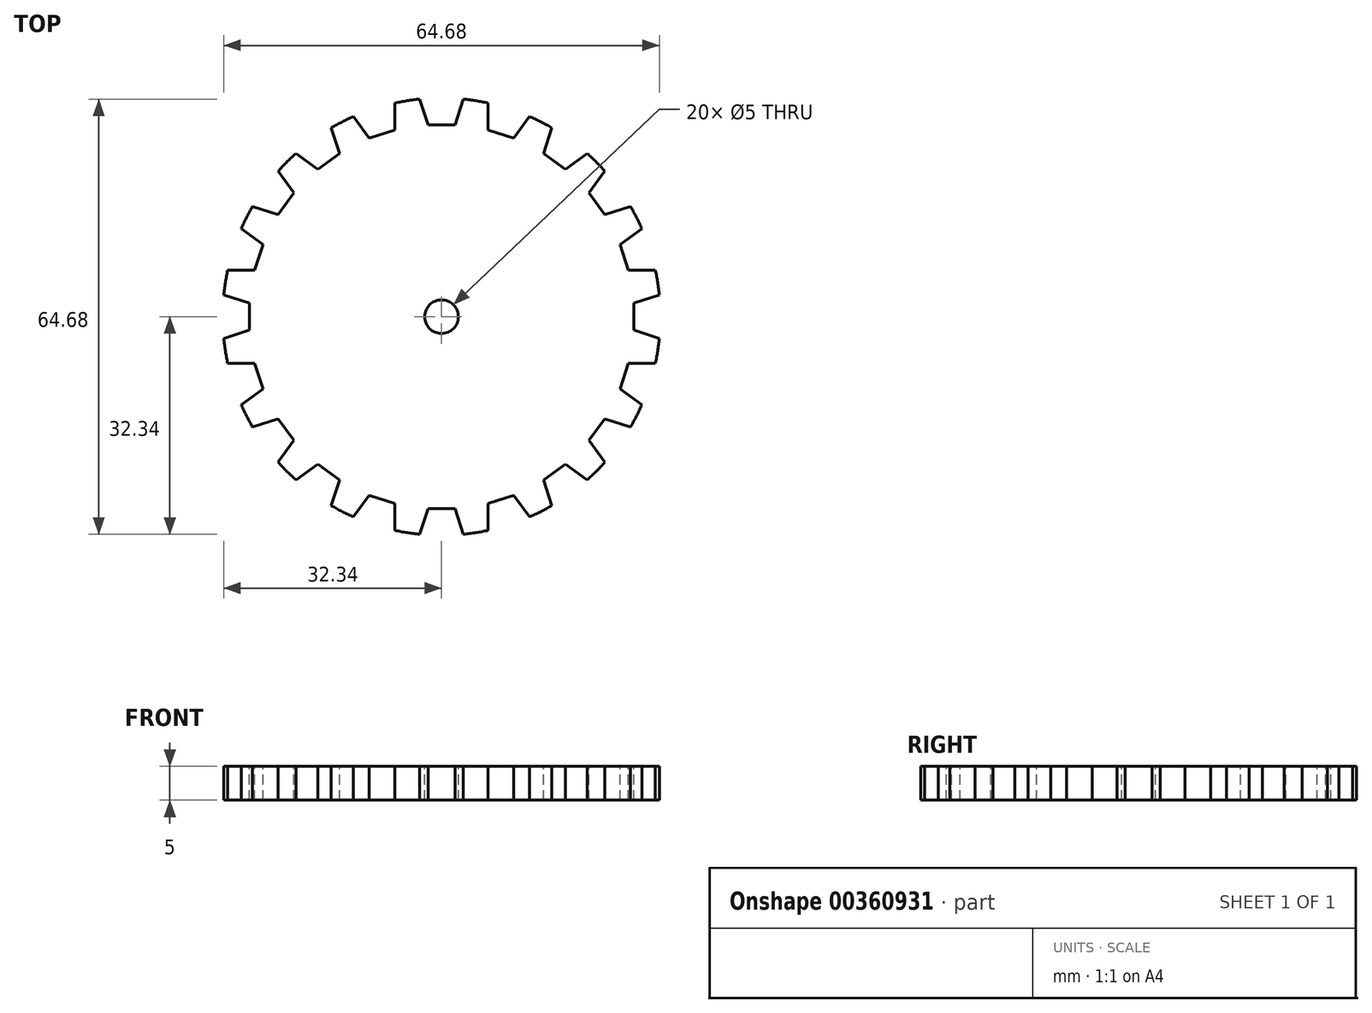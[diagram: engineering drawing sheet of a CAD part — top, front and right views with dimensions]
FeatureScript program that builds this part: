
annotation { "Feature Type Name" : "Feature", "Feature Type Description" : "" }
export const myFeature = defineFeature(function(context is Context, id is Id, definition is map)
    precondition{}
    {
        {
            var Q0;
            Q0=qCreatedBy(makeId("Top.planeOp"),FACE);
            var sketch = newSketch(context, id + "F0", { "sketchPlane" : qUnion([Q0])});
            skCircle(sketch, "E0", {"center": v(0, 0) * mm, "radius": 32.5 * mm});
            skSolve(sketch);
        }
        {
            var Q0;
            Q0=makeQuery(id+"F0.imprint","IMPRINT",FACE,{"disambiguationData":[TD([[makeQuery(id+"F0.imprint","IMPRINT",EDGE,{"derivedFrom":sQuery(id+"F0.wireOp",EDGE,"E0")}),1.0]])]});
            extrude(context, id + "F1", {"entities" : qUnion([Q0]), "depth" : 5 * mm});
        }
        {
            var Q0;
            Q0=makeQuery(id+"F1.opExtrude","CAP_FACE",FACE,{"disambiguationData":[OSD([sQuery(id+"F0.wireOp",EDGE,"E0")])],"isStart":false});
            var sketch = newSketch(context, id + "F2", { "sketchPlane" : qUnion([Q0])});
            skLineSegment(sketch, "E1", {"start": v(3.24, 32.34) * mm, "end": v(2, 28.53) * mm});
            skLineSegment(sketch, "E2", {"start": v(2, 28.53) * mm, "end": v(0, 28.53) * mm});
            skLineSegment(sketch, "E3.MirrorCS", {"start": v(-3.24, 32.34) * mm, "end": v(-2, 28.53) * mm});
            skLineSegment(sketch, "E4.MirrorCS", {"start": v(-2, 28.53) * mm, "end": v(0, 28.53) * mm});
            skArc(sketch, "E5", {"start": v(3.24, 32.34) * mm, "mid": v(0, 34.14) * mm, "end": v(-3.24, 32.34) * mm});
            skSolve(sketch);
        }
        {
            var Q0;
            {var subQ0=sQuery(id+"F2.wireOp",EDGE,"E5");Q0=makeQuery(id+"F2.imprint","IMPRINT",FACE,{"disambiguationData":[TD([[makeQuery(id+"F2.imprint","IMPRINT",EDGE,{"derivedFrom":subQ0}),1.0]])]});}
            var Q1;
            {var subQ1=sQuery(id+"F2.wireOp",EDGE,"E1");Q1=makeQuery(id+"F2.imprint","IMPRINT",FACE,{"disambiguationData":[TD([[makeQuery(id+"F2.imprint","IMPRINT",EDGE,{"derivedFrom":subQ1}),-1.0]])]});}
            extrude(context, id + "F3", {"entities" : qUnion([Q0, Q1]), "operationType" : NewBodyOperationType.ADD, "depth" : 10 * mm});
        }
        {
            var Q0;
            Q0=makeQuery(id+"F1.opExtrude","CAP_FACE",FACE,{"disambiguationData":[OSD([sQuery(id+"F0.wireOp",EDGE,"E0")])],"isStart":false});
            var sketch = newSketch(context, id + "F4", { "sketchPlane" : qUnion([Q0])});
            skCircle(sketch, "E6", {"center": v(0, 0) * mm, "radius": 2.5 * mm});
            skSolve(sketch);
        }
        {
            var Q0;
            Q0=makeQuery(id+"F4.imprint","IMPRINT",FACE,{"disambiguationData":[TD([[makeQuery(id+"F4.imprint","IMPRINT",EDGE,{"derivedFrom":sQuery(id+"F4.wireOp",EDGE,"E6")}),1.0]])]});
            extrude(context, id + "F5", {"entities" : qUnion([Q0]), "operationType" : NewBodyOperationType.REMOVE, "oppositeDirection" : true, "depth" : 25 * mm});
        }
        {
            var Q0;
            Q0=makeQuery(id+"F1.opExtrude","SWEPT_BODY",BODY,{"disambiguationData":[OSD([sQuery(id+"F0.wireOp",EDGE,"E0")])]});
            var Q1;
            Q1=makeQuery(id+"F5.boolean.opBoolean","COPY",FACE,{"derivedFrom":makeQuery(id+"F5.opExtrude","SWEPT_FACE",FACE,{"disambiguationData":[OSD([sQuery(id+"F4.wireOp",EDGE,"E6")])]})});
            circularPattern(context, id + "F6", {"entities" : qUnion([Q0]), "axis" : qUnion([Q1]), "angle" : 360 * degree, "instanceCount" : 20, "equalSpace" : true});
        }
        {
            var Q0;
            Q0=makeQuery(id+"F6.opPattern","COPY",FACE,{"derivedFrom":makeQuery(id+"F3.opExtrude","CAP_FACE",FACE,{"disambiguationData":[OSD([sQuery(id+"F2.wireOp",EDGE,"E1"),sQuery(id+"F2.wireOp",EDGE,"E2"),sQuery(id+"F2.wireOp",EDGE,"E3.MirrorCS"),sQuery(id+"F2.wireOp",EDGE,"E4.MirrorCS"),sQuery(id+"F2.wireOp",EDGE,"E5")])],"isStart":false}),"instanceName":"16"});
            var Q1;
            Q1=makeQuery(id+"F6.opPattern","COPY",FACE,{"derivedFrom":makeQuery(id+"F3.opExtrude","CAP_FACE",FACE,{"disambiguationData":[OSD([sQuery(id+"F2.wireOp",EDGE,"E1"),sQuery(id+"F2.wireOp",EDGE,"E2"),sQuery(id+"F2.wireOp",EDGE,"E3.MirrorCS"),sQuery(id+"F2.wireOp",EDGE,"E4.MirrorCS"),sQuery(id+"F2.wireOp",EDGE,"E5")])],"isStart":false}),"instanceName":"17"});
            var Q2;
            Q2=makeQuery(id+"F6.opPattern","COPY",FACE,{"derivedFrom":makeQuery(id+"F3.opExtrude","CAP_FACE",FACE,{"disambiguationData":[OSD([sQuery(id+"F2.wireOp",EDGE,"E1"),sQuery(id+"F2.wireOp",EDGE,"E2"),sQuery(id+"F2.wireOp",EDGE,"E3.MirrorCS"),sQuery(id+"F2.wireOp",EDGE,"E4.MirrorCS"),sQuery(id+"F2.wireOp",EDGE,"E5")])],"isStart":false}),"instanceName":"18"});
            var Q3;
            Q3=makeQuery(id+"F6.opPattern","COPY",FACE,{"derivedFrom":makeQuery(id+"F3.opExtrude","CAP_FACE",FACE,{"disambiguationData":[OSD([sQuery(id+"F2.wireOp",EDGE,"E1"),sQuery(id+"F2.wireOp",EDGE,"E2"),sQuery(id+"F2.wireOp",EDGE,"E3.MirrorCS"),sQuery(id+"F2.wireOp",EDGE,"E4.MirrorCS"),sQuery(id+"F2.wireOp",EDGE,"E5")])],"isStart":false}),"instanceName":"19"});
            var Q4;
            Q4=makeQuery(id+"F3.opExtrude","CAP_FACE",FACE,{"disambiguationData":[OSD([sQuery(id+"F2.wireOp",EDGE,"E1"),sQuery(id+"F2.wireOp",EDGE,"E2"),sQuery(id+"F2.wireOp",EDGE,"E3.MirrorCS"),sQuery(id+"F2.wireOp",EDGE,"E4.MirrorCS"),sQuery(id+"F2.wireOp",EDGE,"E5")])],"isStart":false});
            var Q5;
            Q5=makeQuery(id+"F6.opPattern","COPY",FACE,{"derivedFrom":makeQuery(id+"F3.opExtrude","CAP_FACE",FACE,{"disambiguationData":[OSD([sQuery(id+"F2.wireOp",EDGE,"E1"),sQuery(id+"F2.wireOp",EDGE,"E2"),sQuery(id+"F2.wireOp",EDGE,"E3.MirrorCS"),sQuery(id+"F2.wireOp",EDGE,"E4.MirrorCS"),sQuery(id+"F2.wireOp",EDGE,"E5")])],"isStart":false}),"instanceName":"1"});
            var Q6;
            Q6=makeQuery(id+"F6.opPattern","COPY",FACE,{"derivedFrom":makeQuery(id+"F3.opExtrude","CAP_FACE",FACE,{"disambiguationData":[OSD([sQuery(id+"F2.wireOp",EDGE,"E1"),sQuery(id+"F2.wireOp",EDGE,"E2"),sQuery(id+"F2.wireOp",EDGE,"E3.MirrorCS"),sQuery(id+"F2.wireOp",EDGE,"E4.MirrorCS"),sQuery(id+"F2.wireOp",EDGE,"E5")])],"isStart":false}),"instanceName":"2"});
            var Q7;
            Q7=makeQuery(id+"F6.opPattern","COPY",FACE,{"derivedFrom":makeQuery(id+"F3.opExtrude","CAP_FACE",FACE,{"disambiguationData":[OSD([sQuery(id+"F2.wireOp",EDGE,"E1"),sQuery(id+"F2.wireOp",EDGE,"E2"),sQuery(id+"F2.wireOp",EDGE,"E3.MirrorCS"),sQuery(id+"F2.wireOp",EDGE,"E4.MirrorCS"),sQuery(id+"F2.wireOp",EDGE,"E5")])],"isStart":false}),"instanceName":"3"});
            var Q8;
            Q8=makeQuery(id+"F6.opPattern","COPY",FACE,{"derivedFrom":makeQuery(id+"F3.opExtrude","CAP_FACE",FACE,{"disambiguationData":[OSD([sQuery(id+"F2.wireOp",EDGE,"E1"),sQuery(id+"F2.wireOp",EDGE,"E2"),sQuery(id+"F2.wireOp",EDGE,"E3.MirrorCS"),sQuery(id+"F2.wireOp",EDGE,"E4.MirrorCS"),sQuery(id+"F2.wireOp",EDGE,"E5")])],"isStart":false}),"instanceName":"4"});
            var Q9;
            Q9=makeQuery(id+"F6.opPattern","COPY",FACE,{"derivedFrom":makeQuery(id+"F3.opExtrude","CAP_FACE",FACE,{"disambiguationData":[OSD([sQuery(id+"F2.wireOp",EDGE,"E1"),sQuery(id+"F2.wireOp",EDGE,"E2"),sQuery(id+"F2.wireOp",EDGE,"E3.MirrorCS"),sQuery(id+"F2.wireOp",EDGE,"E4.MirrorCS"),sQuery(id+"F2.wireOp",EDGE,"E5")])],"isStart":false}),"instanceName":"5"});
            var Q10;
            Q10=makeQuery(id+"F6.opPattern","COPY",FACE,{"derivedFrom":makeQuery(id+"F3.opExtrude","CAP_FACE",FACE,{"disambiguationData":[OSD([sQuery(id+"F2.wireOp",EDGE,"E1"),sQuery(id+"F2.wireOp",EDGE,"E2"),sQuery(id+"F2.wireOp",EDGE,"E3.MirrorCS"),sQuery(id+"F2.wireOp",EDGE,"E4.MirrorCS"),sQuery(id+"F2.wireOp",EDGE,"E5")])],"isStart":false}),"instanceName":"6"});
            var Q11;
            Q11=makeQuery(id+"F6.opPattern","COPY",FACE,{"derivedFrom":makeQuery(id+"F3.opExtrude","CAP_FACE",FACE,{"disambiguationData":[OSD([sQuery(id+"F2.wireOp",EDGE,"E1"),sQuery(id+"F2.wireOp",EDGE,"E2"),sQuery(id+"F2.wireOp",EDGE,"E3.MirrorCS"),sQuery(id+"F2.wireOp",EDGE,"E4.MirrorCS"),sQuery(id+"F2.wireOp",EDGE,"E5")])],"isStart":false}),"instanceName":"7"});
            var Q12;
            Q12=makeQuery(id+"F6.opPattern","COPY",FACE,{"derivedFrom":makeQuery(id+"F3.opExtrude","CAP_FACE",FACE,{"disambiguationData":[OSD([sQuery(id+"F2.wireOp",EDGE,"E1"),sQuery(id+"F2.wireOp",EDGE,"E2"),sQuery(id+"F2.wireOp",EDGE,"E3.MirrorCS"),sQuery(id+"F2.wireOp",EDGE,"E4.MirrorCS"),sQuery(id+"F2.wireOp",EDGE,"E5")])],"isStart":false}),"instanceName":"8"});
            var Q13;
            Q13=makeQuery(id+"F6.opPattern","COPY",FACE,{"derivedFrom":makeQuery(id+"F3.opExtrude","CAP_FACE",FACE,{"disambiguationData":[OSD([sQuery(id+"F2.wireOp",EDGE,"E1"),sQuery(id+"F2.wireOp",EDGE,"E2"),sQuery(id+"F2.wireOp",EDGE,"E3.MirrorCS"),sQuery(id+"F2.wireOp",EDGE,"E4.MirrorCS"),sQuery(id+"F2.wireOp",EDGE,"E5")])],"isStart":false}),"instanceName":"9"});
            var Q14;
            Q14=makeQuery(id+"F6.opPattern","COPY",FACE,{"derivedFrom":makeQuery(id+"F3.opExtrude","CAP_FACE",FACE,{"disambiguationData":[OSD([sQuery(id+"F2.wireOp",EDGE,"E1"),sQuery(id+"F2.wireOp",EDGE,"E2"),sQuery(id+"F2.wireOp",EDGE,"E3.MirrorCS"),sQuery(id+"F2.wireOp",EDGE,"E4.MirrorCS"),sQuery(id+"F2.wireOp",EDGE,"E5")])],"isStart":false}),"instanceName":"10"});
            var Q15;
            Q15=makeQuery(id+"F6.opPattern","COPY",FACE,{"derivedFrom":makeQuery(id+"F3.opExtrude","CAP_FACE",FACE,{"disambiguationData":[OSD([sQuery(id+"F2.wireOp",EDGE,"E1"),sQuery(id+"F2.wireOp",EDGE,"E2"),sQuery(id+"F2.wireOp",EDGE,"E3.MirrorCS"),sQuery(id+"F2.wireOp",EDGE,"E4.MirrorCS"),sQuery(id+"F2.wireOp",EDGE,"E5")])],"isStart":false}),"instanceName":"11"});
            var Q16;
            Q16=makeQuery(id+"F6.opPattern","COPY",FACE,{"derivedFrom":makeQuery(id+"F3.opExtrude","CAP_FACE",FACE,{"disambiguationData":[OSD([sQuery(id+"F2.wireOp",EDGE,"E1"),sQuery(id+"F2.wireOp",EDGE,"E2"),sQuery(id+"F2.wireOp",EDGE,"E3.MirrorCS"),sQuery(id+"F2.wireOp",EDGE,"E4.MirrorCS"),sQuery(id+"F2.wireOp",EDGE,"E5")])],"isStart":false}),"instanceName":"12"});
            var Q17;
            Q17=makeQuery(id+"F6.opPattern","COPY",FACE,{"derivedFrom":makeQuery(id+"F3.opExtrude","CAP_FACE",FACE,{"disambiguationData":[OSD([sQuery(id+"F2.wireOp",EDGE,"E1"),sQuery(id+"F2.wireOp",EDGE,"E2"),sQuery(id+"F2.wireOp",EDGE,"E3.MirrorCS"),sQuery(id+"F2.wireOp",EDGE,"E4.MirrorCS"),sQuery(id+"F2.wireOp",EDGE,"E5")])],"isStart":false}),"instanceName":"13"});
            var Q18;
            Q18=makeQuery(id+"F6.opPattern","COPY",FACE,{"derivedFrom":makeQuery(id+"F3.opExtrude","CAP_FACE",FACE,{"disambiguationData":[OSD([sQuery(id+"F2.wireOp",EDGE,"E1"),sQuery(id+"F2.wireOp",EDGE,"E2"),sQuery(id+"F2.wireOp",EDGE,"E3.MirrorCS"),sQuery(id+"F2.wireOp",EDGE,"E4.MirrorCS"),sQuery(id+"F2.wireOp",EDGE,"E5")])],"isStart":false}),"instanceName":"14"});
            var Q19;
            Q19=makeQuery(id+"F6.opPattern","COPY",FACE,{"derivedFrom":makeQuery(id+"F3.opExtrude","CAP_FACE",FACE,{"disambiguationData":[OSD([sQuery(id+"F2.wireOp",EDGE,"E1"),sQuery(id+"F2.wireOp",EDGE,"E2"),sQuery(id+"F2.wireOp",EDGE,"E3.MirrorCS"),sQuery(id+"F2.wireOp",EDGE,"E4.MirrorCS"),sQuery(id+"F2.wireOp",EDGE,"E5")])],"isStart":false}),"instanceName":"15"});
            extrude(context, id + "F7", {"entities" : qUnion([Q0, Q1, Q2, Q3, Q4, Q5, Q6, Q7, Q8, Q9, Q10, Q11, Q12, Q13, Q14, Q15, Q16, Q17, Q18, Q19]), "operationType" : NewBodyOperationType.REMOVE, "oppositeDirection" : true, "depth" : 25 * mm});
        }
    });
